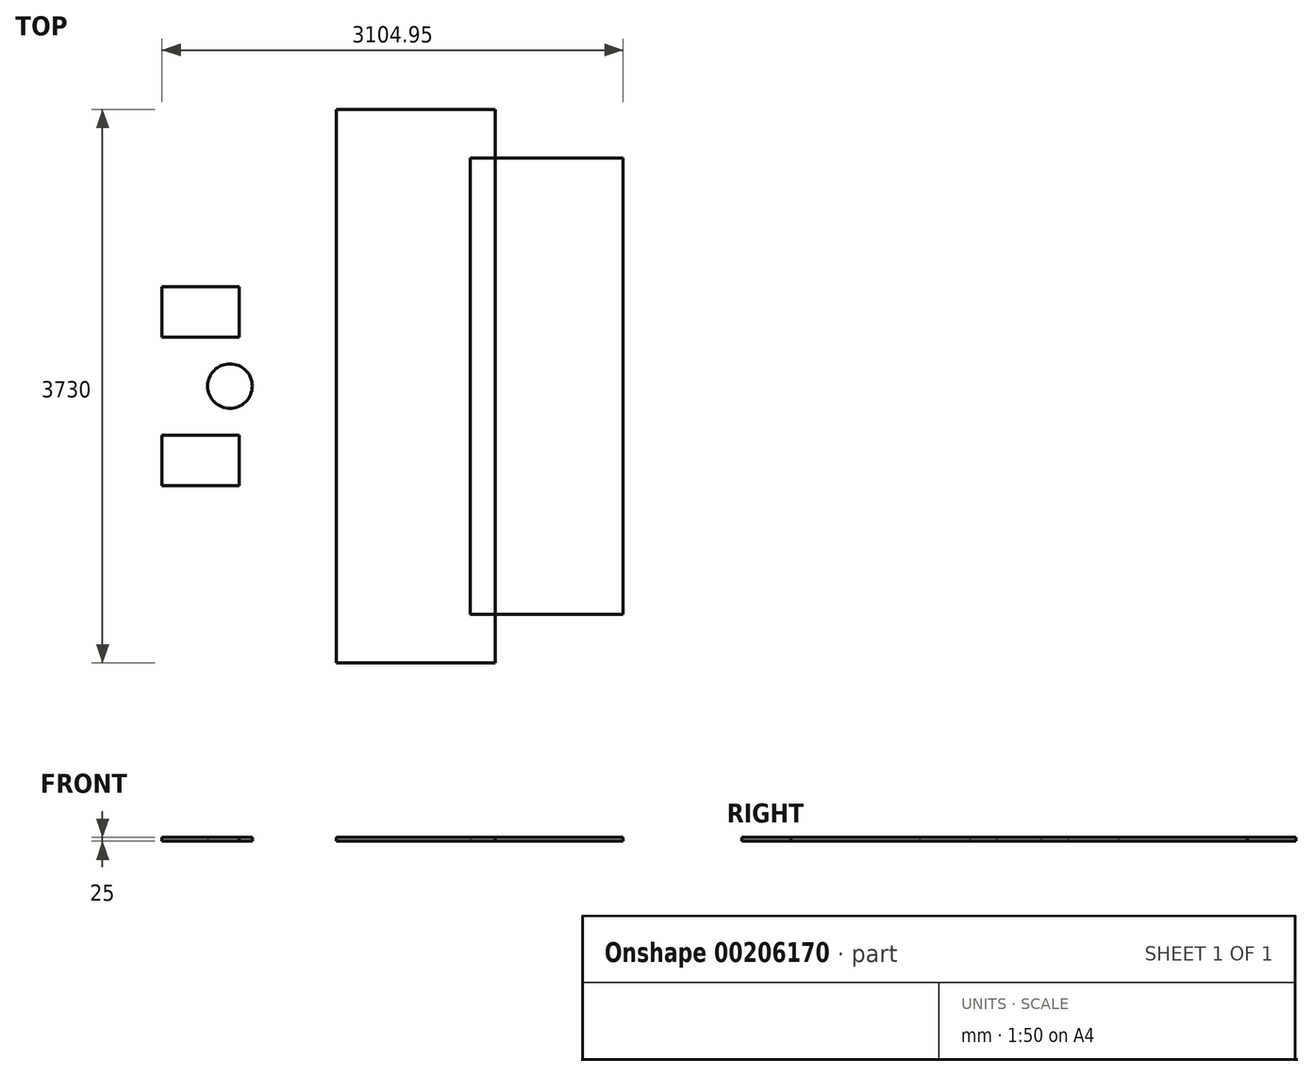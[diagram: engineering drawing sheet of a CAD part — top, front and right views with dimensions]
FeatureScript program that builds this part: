
annotation { "Feature Type Name" : "Feature", "Feature Type Description" : "" }
export const myFeature = defineFeature(function(context is Context, id is Id, definition is map)
    precondition{}
    {
        {
            var Q0;
            Q0=qCreatedBy(makeId("Top.planeOp"),FACE);
            var sketch = newSketch(context, id + "F0", { "sketchPlane" : qUnion([Q0])});
            skLineSegment(sketch, "E0.bottom", {"start": v(-18060.05, -1536.7) * mm, "end": v(-19088.75, -1536.7) * mm});
            skLineSegment(sketch, "E0.top", {"start": v(-18060.05, 1536.7) * mm, "end": v(-19088.75, 1536.7) * mm});
            skLineSegment(sketch, "E0.left", {"start": v(-18060.05, -1536.7) * mm, "end": v(-18060.05, 1536.7) * mm});
            skLineSegment(sketch, "E0.right", {"start": v(-19088.75, -1536.7) * mm, "end": v(-19088.75, 1536.7) * mm});
            skPoint(sketch, "E0.middle", {"position": v(-18574.4, 0) * mm});
            skLineSegment(sketch, "E1.bottom", {"start": v(1809.1, -1460.5) * mm, "end": v(462.9, -1460.5) * mm});
            skLineSegment(sketch, "E1.top", {"start": v(1809.1, 1460.5) * mm, "end": v(462.9, 1460.5) * mm});
            skLineSegment(sketch, "E1.left", {"start": v(1809.1, -1460.5) * mm, "end": v(1809.1, 1460.5) * mm});
            skLineSegment(sketch, "E1.right", {"start": v(462.9, -1460.5) * mm, "end": v(462.9, 1460.5) * mm});
            skPoint(sketch, "E1.middle", {"position": v(1136, 0) * mm});
            skLineSegment(sketch, "E2", {"start": v(-18574.4, 0) * mm, "end": v(1136, 0) * mm});
            skCircle(sketch, "E3", {"center": v(-20707.4, 0) * mm, "radius": 150 * mm});
            skLineSegment(sketch, "E4.bottom", {"start": v(2402, 50) * mm, "end": v(1902, 50) * mm});
            skLineSegment(sketch, "E4.top", {"start": v(2402, 550) * mm, "end": v(1902, 550) * mm});
            skLineSegment(sketch, "E4.left", {"start": v(2402, 50) * mm, "end": v(2402, 550) * mm});
            skLineSegment(sketch, "E4.right", {"start": v(1902, 50) * mm, "end": v(1902, 550) * mm});
            skPoint(sketch, "E4.middle", {"position": v(2152, 300) * mm});
            skSolve(sketch);
        }
        {
            var Q0;
            Q0=qCreatedBy(makeId("Top.planeOp"),FACE);
            var sketch = newSketch(context, id + "F1", { "sketchPlane" : qUnion([Q0])});
            skLineSegment(sketch, "E5.bottom", {"start": v(450, -1865) * mm, "end": v(-450, -1865) * mm});
            skLineSegment(sketch, "E5.top", {"start": v(450, 1865) * mm, "end": v(-450, 1865) * mm});
            skLineSegment(sketch, "E5.left", {"start": v(450, -1865) * mm, "end": v(450, 1865) * mm});
            skLineSegment(sketch, "E5.right", {"start": v(-450, -1865) * mm, "end": v(-450, 1865) * mm});
            skPoint(sketch, "E5.middle", {"position": v(0, 0) * mm});
            skLineSegment(sketch, "E6.bottom", {"start": v(600, 1030) * mm, "end": v(3050, 1030) * mm});
            skLineSegment(sketch, "E6.top", {"start": v(600, 1972) * mm, "end": v(3050, 1972) * mm});
            skLineSegment(sketch, "E6.left", {"start": v(600, 1030) * mm, "end": v(600, 1972) * mm});
            skLineSegment(sketch, "E6.right", {"start": v(3050, 1030) * mm, "end": v(3050, 1972) * mm});
            skPoint(sketch, "E6.middle", {"position": v(1825, 1501) * mm});
            skLineSegment(sketch, "E7.bottom", {"start": v(2402, 50) * mm, "end": v(1902, 50) * mm});
            skLineSegment(sketch, "E7.top", {"start": v(2402, 550) * mm, "end": v(1902, 550) * mm});
            skLineSegment(sketch, "E7.left", {"start": v(2402, 50) * mm, "end": v(2402, 550) * mm});
            skLineSegment(sketch, "E7.right", {"start": v(1902, 50) * mm, "end": v(1902, 550) * mm});
            skPoint(sketch, "E7.middle", {"position": v(2152, 300) * mm});
            skLineSegment(sketch, "E8.bottom", {"start": v(2637, -1402.5) * mm, "end": v(1132, -1402.5) * mm});
            skLineSegment(sketch, "E8.top", {"start": v(2637, -1277.5) * mm, "end": v(1132, -1277.5) * mm});
            skLineSegment(sketch, "E8.left", {"start": v(2637, -1402.5) * mm, "end": v(2637, -1277.5) * mm});
            skLineSegment(sketch, "E8.right", {"start": v(1132, -1402.5) * mm, "end": v(1132, -1277.5) * mm});
            skPoint(sketch, "E8.middle", {"position": v(1884.5, -1340) * mm});
            skLineSegment(sketch, "E9.bottom", {"start": v(2661.94, 727.5) * mm, "end": v(1132, 727.5) * mm});
            skLineSegment(sketch, "E9.top", {"start": v(2661.94, 852.5) * mm, "end": v(1132, 852.5) * mm});
            skLineSegment(sketch, "E9.left", {"start": v(2661.94, 727.5) * mm, "end": v(2661.94, 852.5) * mm});
            skLineSegment(sketch, "E9.right", {"start": v(1132, 727.5) * mm, "end": v(1132, 852.5) * mm});
            skPoint(sketch, "E9.middle", {"position": v(1896.97, 790) * mm});
            skLineSegment(sketch, "E10.bottom", {"start": v(-18920, -1865) * mm, "end": v(-19990, -1865) * mm});
            skLineSegment(sketch, "E10.top", {"start": v(-18920, 1865) * mm, "end": v(-19990, 1865) * mm});
            skLineSegment(sketch, "E10.left", {"start": v(-18920, -1865) * mm, "end": v(-18920, 1865) * mm});
            skLineSegment(sketch, "E10.right", {"start": v(-19990, -1865) * mm, "end": v(-19990, 1865) * mm});
            skPoint(sketch, "E10.middle", {"position": v(-19455, 0) * mm});
            skLineSegment(sketch, "E11.bottom", {"start": v(-20645, 330) * mm, "end": v(-21165, 330) * mm});
            skLineSegment(sketch, "E11.top", {"start": v(-20645, 670) * mm, "end": v(-21165, 670) * mm});
            skLineSegment(sketch, "E11.left", {"start": v(-20645, 330) * mm, "end": v(-20645, 670) * mm});
            skLineSegment(sketch, "E11.right", {"start": v(-21165, 330) * mm, "end": v(-21165, 670) * mm});
            skPoint(sketch, "E11.middle", {"position": v(-20905, 500) * mm});
            skLineSegment(sketch, "E12.bottom", {"start": v(-20645, -670) * mm, "end": v(-21165, -670) * mm});
            skLineSegment(sketch, "E12.top", {"start": v(-20645, -330) * mm, "end": v(-21165, -330) * mm});
            skLineSegment(sketch, "E12.left", {"start": v(-20645, -670) * mm, "end": v(-20645, -330) * mm});
            skLineSegment(sketch, "E12.right", {"start": v(-21165, -670) * mm, "end": v(-21165, -330) * mm});
            skPoint(sketch, "E12.middle", {"position": v(-20905, -500) * mm});
            skPoint(sketch, "E13", {"position": v(-20905, -330) * mm});
            skLineSegment(sketch, "E14", {"start": v(0, 0) * mm, "end": v(-19455, 0) * mm});
            skCircle(sketch, "E15", {"center": v(1202, -1340) * mm, "radius": 15 * mm});
            skCircle(sketch, "E16", {"center": v(335, -1866.07) * mm, "radius": 15 * mm});
            skCircle(sketch, "E17", {"center": v(1202, 790) * mm, "radius": 15 * mm});
            skSolve(sketch);
        }
        {
            var Q0;
            {var subQ3=sQuery(id+"F1.wireOp",EDGE,"E10.bottom");Q0=makeQuery(id+"F1.imprint","IMPRINT",FACE,{"disambiguationData":[TD([[makeQuery(id+"F1.imprint","IMPRINT",EDGE,{"derivedFrom":subQ3}),-1.0]])]});}
            var Q1;
            {var subQ3=sQuery(id+"F0.wireOp",EDGE,"E0.bottom");Q1=makeQuery(id+"F0.imprint","IMPRINT",FACE,{"disambiguationData":[TD([[makeQuery(id+"F0.imprint","IMPRINT",EDGE,{"derivedFrom":subQ3}),-1.0]])]});}
            var Q2;
            Q2=makeQuery(id+"F1.imprint","IMPRINT",FACE,{"disambiguationData":[TD([[makeQuery(id+"F1.imprint","IMPRINT",EDGE,{"derivedFrom":sQuery(id+"F1.wireOp",EDGE,"E12.bottom")}),-1.0]])]});
            var Q3;
            Q3=makeQuery(id+"F1.imprint","IMPRINT",FACE,{"disambiguationData":[TD([[makeQuery(id+"F1.imprint","IMPRINT",EDGE,{"derivedFrom":sQuery(id+"F1.wireOp",EDGE,"E11.bottom")}),-1.0]])]});
            var Q4;
            Q4=makeQuery(id+"F0.imprint","IMPRINT",FACE,{"disambiguationData":[TD([[makeQuery(id+"F0.imprint","IMPRINT",EDGE,{"derivedFrom":sQuery(id+"F0.wireOp",EDGE,"E3")}),1.0]])]});
            extrude(context, id + "F2", {"entities" : qUnion([Q0, Q1, Q2, Q3, Q4]), "depth" : 25 * mm});
        }
    });
